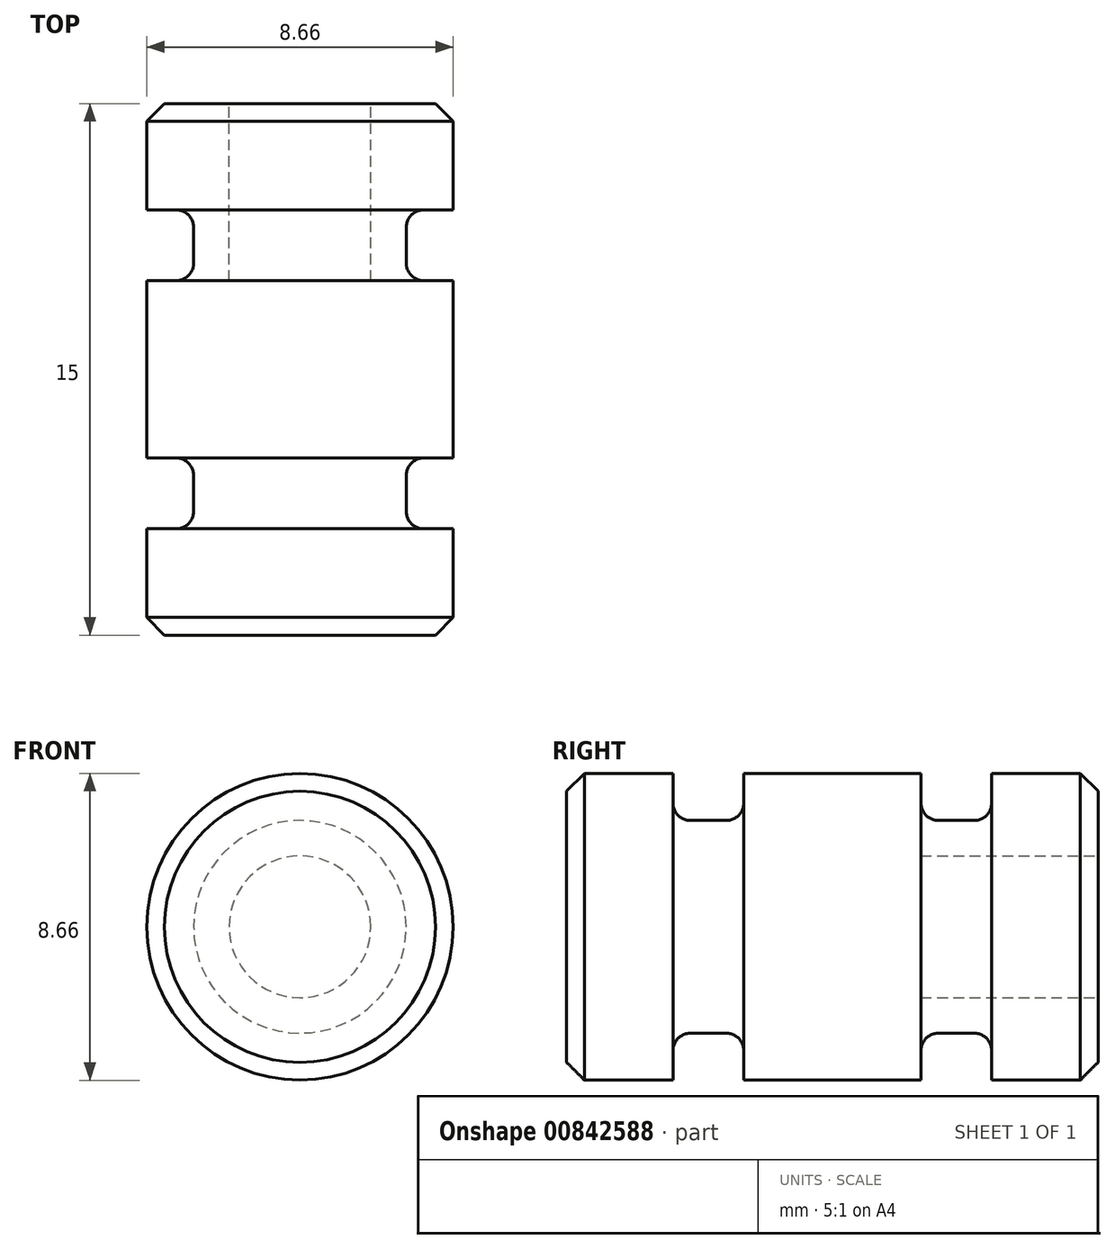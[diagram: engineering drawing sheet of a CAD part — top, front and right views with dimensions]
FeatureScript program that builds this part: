
annotation { "Feature Type Name" : "Feature", "Feature Type Description" : "" }
export const myFeature = defineFeature(function(context is Context, id is Id, definition is map)
    precondition{}
    {
        {
            var Q0;
            Q0=qCreatedBy(makeId("Front.planeOp"),FACE);
            var sketch = newSketch(context, id + "F0", { "sketchPlane" : qUnion([Q0])});
            skCircle(sketch, "E0", {"center": v(0, 0) * mm, "radius": 4.32 * mm});
            skSolve(sketch);
        }
        {
            var Q0;
            Q0 = qSketchRegion(id + "F0", true);
            extrude(context, id + "F1", {"entities" : qUnion([Q0]), "oppositeDirection" : true, "depth" : 15 * mm, "offsetDistance" : 25 * mm});
        }
        {
            var Q0;
            Q0=qCreatedBy(makeId("Front.planeOp"),FACE);
            cPlane(context, id + "F2", {"entities" : qUnion([Q0]), "cplaneType" : CPlaneType.OFFSET, "offset" : 3 * mm, "oppositeDirection" : true, "width" : 150 * mm, "height" : 150 * mm});
        }
        {
            var Q0;
            Q0=qCreatedBy(makeId("Front.planeOp"),FACE);
            cPlane(context, id + "F3", {"entities" : qUnion([Q0]), "cplaneType" : CPlaneType.OFFSET, "offset" : 10 * mm, "oppositeDirection" : true, "width" : 150 * mm, "height" : 150 * mm});
        }
        {
            var Q0;
            Q0=qCreatedBy(id+"F2.planeOp",FACE);
            var sketch = newSketch(context, id + "F4", { "sketchPlane" : qUnion([Q0])});
            skCircle(sketch, "E1", {"center": v(0, 0) * mm, "radius": 4.5 * mm});
            skCircle(sketch, "E2", {"center": v(0, 0) * mm, "radius": 3 * mm});
            skSolve(sketch);
        }
        {
            var Q0;
            Q0 = qSketchRegion(id + "F4", true);
            extrude(context, id + "F5", {"entities" : qUnion([Q0]), "operationType" : NewBodyOperationType.REMOVE, "oppositeDirection" : true, "depth" : 2 * mm, "offsetDistance" : 25 * mm});
        }
        {
            var Q0;
            Q0=qCreatedBy(id+"F3.planeOp",FACE);
            var sketch = newSketch(context, id + "F6", { "sketchPlane" : qUnion([Q0])});
            skCircle(sketch, "E3", {"center": v(0, 0) * mm, "radius": 3 * mm});
            skCircle(sketch, "E4", {"center": v(0, 0) * mm, "radius": 4.5 * mm});
            skSolve(sketch);
        }
        {
            var Q0;
            Q0 = qSketchRegion(id + "F6", true);
            extrude(context, id + "F7", {"entities" : qUnion([Q0]), "operationType" : NewBodyOperationType.REMOVE, "oppositeDirection" : true, "depth" : 2 * mm, "offsetDistance" : 25 * mm});
        }
        {
            var Q0;
            Q0=makeQuery(id+"F1.opExtrude","CAP_EDGE",EDGE,{"disambiguationData":[OSD([sQuery(id+"F0.wireOp",EDGE,"E0")])],"isStart":true});
            var Q1;
            Q1=makeQuery(id+"F1.opExtrude","CAP_EDGE",EDGE,{"disambiguationData":[OSD([sQuery(id+"F0.wireOp",EDGE,"E0")])],"isStart":false});
            chamfer(context, id + "F8", {"entities" : qUnion([Q0, Q1]), "width" : 0.5 * mm, "tangentPropagation" : true});
        }
        {
            var Q0;
            Q0=makeQuery(id+"F5.boolean.opBoolean","COPY",EDGE,{"derivedFrom":makeQuery(id+"F5.opExtrude","CAP_EDGE",EDGE,{"disambiguationData":[OSD([sQuery(id+"F4.wireOp",EDGE,"E2")])],"isStart":false})});
            var Q1;
            Q1=makeQuery(id+"F7.boolean.opBoolean","COPY",EDGE,{"derivedFrom":makeQuery(id+"F7.opExtrude","CAP_EDGE",EDGE,{"disambiguationData":[OSD([sQuery(id+"F6.wireOp",EDGE,"E3")])],"isStart":false})});
            var Q2;
            Q2=makeQuery(id+"F7.boolean.opBoolean","COPY",EDGE,{"derivedFrom":makeQuery(id+"F7.opExtrude","CAP_EDGE",EDGE,{"disambiguationData":[OSD([sQuery(id+"F6.wireOp",EDGE,"E3")])],"isStart":true})});
            var Q3;
            Q3=makeQuery(id+"F5.boolean.opBoolean","COPY",EDGE,{"derivedFrom":makeQuery(id+"F5.opExtrude","CAP_EDGE",EDGE,{"disambiguationData":[OSD([sQuery(id+"F4.wireOp",EDGE,"E2")])],"isStart":true})});
            fillet(context, id + "F9", {"entities" : qUnion([Q0, Q1, Q2, Q3]), "radius" : 0.5 * mm, "tangentPropagation" : true, "allowEdgeOverflow" : false});
        }
        {
            var Q0;
            Q0=makeQuery(id+"F1.opExtrude","CAP_FACE",FACE,{"disambiguationData":[OSD([sQuery(id+"F0.wireOp",EDGE,"E0")])],"isStart":false});
            var sketch = newSketch(context, id + "F10", { "sketchPlane" : qUnion([Q0])});
            skCircle(sketch, "E5", {"center": v(0, 0) * mm, "radius": 2 * mm});
            skSolve(sketch);
        }
        {
            var Q0;
            Q0 = qSketchRegion(id + "F10", true);
            extrude(context, id + "F11", {"entities" : qUnion([Q0]), "operationType" : NewBodyOperationType.REMOVE, "oppositeDirection" : true, "depth" : 5 * mm, "offsetDistance" : 25 * mm});
        }
    });
